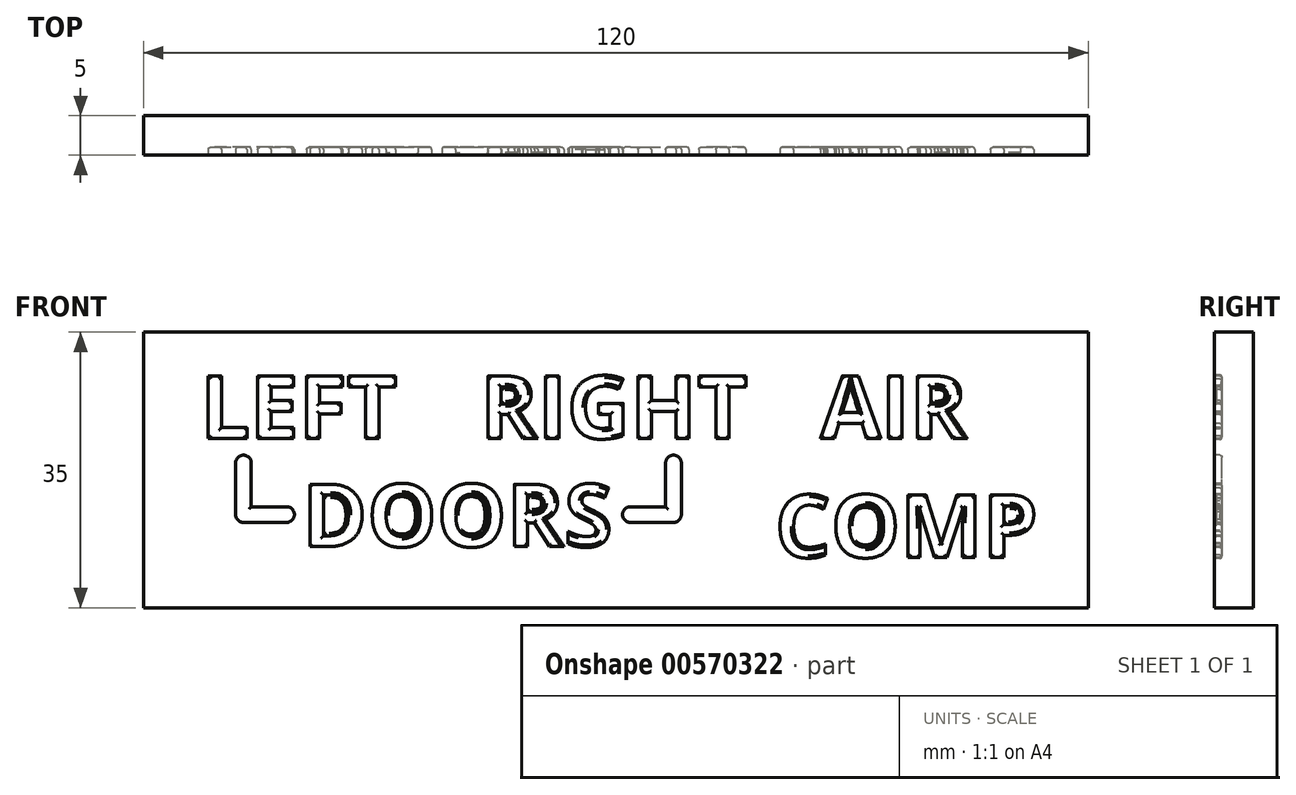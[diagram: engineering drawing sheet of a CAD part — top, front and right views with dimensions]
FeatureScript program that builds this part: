
annotation { "Feature Type Name" : "Feature", "Feature Type Description" : "" }
export const myFeature = defineFeature(function(context is Context, id is Id, definition is map)
    precondition{}
    {
        {
            var Q0;
            Q0=qCreatedBy(makeId("Front.planeOp"),FACE);
            var sketch = newSketch(context, id + "F0", { "sketchPlane" : qUnion([Q0])});
            skLineSegment(sketch, "E0.bottom", {"start": v(60, -17.5) * mm, "end": v(-60, -17.5) * mm});
            skLineSegment(sketch, "E0.top", {"start": v(60, 17.5) * mm, "end": v(-60, 17.5) * mm});
            skLineSegment(sketch, "E0.left", {"start": v(60, -17.5) * mm, "end": v(60, 17.5) * mm});
            skLineSegment(sketch, "E0.right", {"start": v(-60, -17.5) * mm, "end": v(-60, 17.5) * mm});
            skPoint(sketch, "E0.middle", {"position": v(0, 0) * mm});
            skLineSegment(sketch, "E1", {"start": v(-40, 69.11) * mm, "end": v(-40, -88.68) * mm, "construction": true});
            skLineSegment(sketch, "E2", {"start": v(37, 69.11) * mm, "end": v(37, -90.14) * mm, "construction": true});
            skLineSegment(sketch, "E3", {"start": v(0, 69.11) * mm, "end": v(0, -90.14) * mm, "construction": true});
            skSolve(sketch);
        }
        {
            var Q0;
            Q0=makeQuery(id+"F0.imprint","IMPRINT",FACE,{"disambiguationData":[TD([[makeQuery(id+"F0.imprint","IMPRINT",EDGE,{"derivedFrom":sQuery(id+"F0.wireOp",EDGE,"E0.bottom")}),-1.0]])]});
            extrude(context, id + "F1", {"entities" : qUnion([Q0]), "depth" : 5 * mm, "offsetDistance" : 25 * mm});
        }
        {
            var Q0;
            Q0=makeQuery(id+"F1.opExtrude","CAP_FACE",FACE,{"disambiguationData":[OSD([sQuery(id+"F0.wireOp",EDGE,"E0.bottom"),sQuery(id+"F0.wireOp",EDGE,"E0.top"),sQuery(id+"F0.wireOp",EDGE,"E0.left"),sQuery(id+"F0.wireOp",EDGE,"E0.right")])],"isStart":false});
            var sketch = newSketch(context, id + "F2", { "sketchPlane" : qUnion([Q0])});
            skText(sketch, "E4", { "text": "LEFT", "fontName": "OpenSans-Bold.ttf"});
            skText(sketch, "E5", { "text": "DOORS", "fontName": "OpenSans-Bold.ttf"});
            skLineSegment(sketch, "E6", {"start": v(-40, -17.5) * mm, "end": v(0, -17.5) * mm, "construction": true});
            skPoint(sketch, "E7", {"position": v(-20, -17.5) * mm});
            skText(sketch, "E8", { "text": "RIGHT", "fontName": "OpenSans-Bold.ttf"});
            skText(sketch, "E9", { "text": "  AIR\nCOMP", "fontName": "OpenSans-Bold.ttf"});
            skLineSegment(sketch, "E10", {"start": v(-20, -43.15) * mm, "end": v(-20, 45.34) * mm, "construction": true});
            skLineSegment(sketch, "E11", {"start": v(-41.84, -5.67) * mm, "end": v(-47.32, -5.67) * mm});
            skLineSegment(sketch, "E12", {"start": v(-47.32, -5.67) * mm, "end": v(-47.32, 0.89) * mm});
            skLineSegment(sketch, "E13.MirrorCS", {"start": v(7.32, -5.67) * mm, "end": v(7.32, 0.89) * mm});
            skLineSegment(sketch, "E14.MirrorCS", {"start": v(1.84, -5.67) * mm, "end": v(7.32, -5.67) * mm});
            skArc(sketch, "E15.0.startCap", {"start": v(-41.84, -4.67) * mm, "mid": v(-40.84, -5.67) * mm, "end": v(-41.84, -6.67) * mm});
            skArc(sketch, "E15.0.endCap", {"start": v(-47.32, -6.67) * mm, "mid": v(-48.32, -5.67) * mm, "end": v(-47.32, -4.67) * mm});
            skLineSegment(sketch, "E15.0.left", {"start": v(-41.84, -6.67) * mm, "end": v(-47.32, -6.67) * mm});
            skLineSegment(sketch, "E15.0.right", {"start": v(-41.84, -4.67) * mm, "end": v(-47.32, -4.67) * mm});
            skArc(sketch, "E15.1.startCap", {"start": v(-46.32, -5.67) * mm, "mid": v(-47.32, -6.67) * mm, "end": v(-48.32, -5.67) * mm});
            skArc(sketch, "E15.1.endCap", {"start": v(-48.32, 0.89) * mm, "mid": v(-47.32, 1.89) * mm, "end": v(-46.32, 0.89) * mm});
            skLineSegment(sketch, "E15.1.left", {"start": v(-48.32, -5.67) * mm, "end": v(-48.32, 0.89) * mm});
            skLineSegment(sketch, "E15.1.right", {"start": v(-46.32, -5.67) * mm, "end": v(-46.32, 0.89) * mm});
            skArc(sketch, "E15.2.startCap", {"start": v(1.84, -6.67) * mm, "mid": v(0.84, -5.67) * mm, "end": v(1.84, -4.67) * mm});
            skArc(sketch, "E15.2.endCap", {"start": v(7.32, -4.67) * mm, "mid": v(8.32, -5.67) * mm, "end": v(7.32, -6.67) * mm});
            skLineSegment(sketch, "E15.2.left", {"start": v(1.84, -4.67) * mm, "end": v(7.32, -4.67) * mm});
            skLineSegment(sketch, "E15.2.right", {"start": v(1.84, -6.67) * mm, "end": v(7.32, -6.67) * mm});
            skArc(sketch, "E15.3.startCap", {"start": v(8.32, -5.67) * mm, "mid": v(7.32, -6.67) * mm, "end": v(6.32, -5.67) * mm});
            skArc(sketch, "E15.3.endCap", {"start": v(6.32, 0.89) * mm, "mid": v(7.32, 1.89) * mm, "end": v(8.32, 0.89) * mm});
            skLineSegment(sketch, "E15.3.left", {"start": v(6.32, -5.67) * mm, "end": v(6.32, 0.89) * mm});
            skLineSegment(sketch, "E15.3.right", {"start": v(8.32, -5.67) * mm, "end": v(8.32, 0.89) * mm});
            const initialGuessF2  = {"E4": [-0.05277, 0.004, 1, 0, 0.008], "E5": [-0.03982, -0.00974, 1, 0, 0.008], "E8": [-0.01725, 0.004, 1, 0, 0.008], "E9": [0.0202, 0.004, 1, 0, 0.008]};
            skSetInitialGuess(sketch, initialGuessF2);
            skSolve(sketch);
        }
        {
            var Q0;
            Q0 = qSketchRegion(id + "F2", true);
            extrude(context, id + "F3", {"entities" : qUnion([Q0]), "operationType" : NewBodyOperationType.REMOVE, "oppositeDirection" : true, "depth" : 1 * mm, "offsetDistance" : 25 * mm});
        }
        {
            var Q0;
            Q0=makeQuery(id+"F3.boolean.opBoolean","COPY",FACE,{"derivedFrom":makeQuery(id+"F3.opExtrude","CAP_FACE",FACE,{"disambiguationData":[OSD([sQuery(id+"F2.wireOp",EDGE,"E4.sketch_text.stroke-0"),sQuery(id+"F2.wireOp",EDGE,"E4.sketch_text.stroke-1"),sQuery(id+"F2.wireOp",EDGE,"E4.sketch_text.stroke-2"),sQuery(id+"F2.wireOp",EDGE,"E4.sketch_text.stroke-3"),sQuery(id+"F2.wireOp",EDGE,"E4.sketch_text.stroke-4"),sQuery(id+"F2.wireOp",EDGE,"E4.sketch_text.stroke-5")])],"isStart":false})});
            var Q1;
            Q1=makeQuery(id+"F3.boolean.opBoolean","COPY",FACE,{"derivedFrom":makeQuery(id+"F3.opExtrude","CAP_FACE",FACE,{"disambiguationData":[OSD([sQuery(id+"F2.wireOp",EDGE,"E4.sketch_text.stroke-6"),sQuery(id+"F2.wireOp",EDGE,"E4.sketch_text.stroke-7"),sQuery(id+"F2.wireOp",EDGE,"E4.sketch_text.stroke-8"),sQuery(id+"F2.wireOp",EDGE,"E4.sketch_text.stroke-9"),sQuery(id+"F2.wireOp",EDGE,"E4.sketch_text.stroke-10"),sQuery(id+"F2.wireOp",EDGE,"E4.sketch_text.stroke-11"),sQuery(id+"F2.wireOp",EDGE,"E4.sketch_text.stroke-12"),sQuery(id+"F2.wireOp",EDGE,"E4.sketch_text.stroke-13"),sQuery(id+"F2.wireOp",EDGE,"E4.sketch_text.stroke-14"),sQuery(id+"F2.wireOp",EDGE,"E4.sketch_text.stroke-15"),sQuery(id+"F2.wireOp",EDGE,"E4.sketch_text.stroke-16"),sQuery(id+"F2.wireOp",EDGE,"E4.sketch_text.stroke-17")])],"isStart":false})});
            var Q2;
            Q2=makeQuery(id+"F3.boolean.opBoolean","COPY",FACE,{"derivedFrom":makeQuery(id+"F3.opExtrude","CAP_FACE",FACE,{"disambiguationData":[OSD([sQuery(id+"F2.wireOp",EDGE,"E4.sketch_text.stroke-18"),sQuery(id+"F2.wireOp",EDGE,"E4.sketch_text.stroke-19"),sQuery(id+"F2.wireOp",EDGE,"E4.sketch_text.stroke-20"),sQuery(id+"F2.wireOp",EDGE,"E4.sketch_text.stroke-21"),sQuery(id+"F2.wireOp",EDGE,"E4.sketch_text.stroke-22"),sQuery(id+"F2.wireOp",EDGE,"E4.sketch_text.stroke-23"),sQuery(id+"F2.wireOp",EDGE,"E4.sketch_text.stroke-24"),sQuery(id+"F2.wireOp",EDGE,"E4.sketch_text.stroke-25"),sQuery(id+"F2.wireOp",EDGE,"E4.sketch_text.stroke-26"),sQuery(id+"F2.wireOp",EDGE,"E4.sketch_text.stroke-27")])],"isStart":false})});
            var Q3;
            Q3=makeQuery(id+"F3.boolean.opBoolean","COPY",FACE,{"derivedFrom":makeQuery(id+"F3.opExtrude","CAP_FACE",FACE,{"disambiguationData":[OSD([sQuery(id+"F2.wireOp",EDGE,"E4.sketch_text.stroke-28"),sQuery(id+"F2.wireOp",EDGE,"E4.sketch_text.stroke-29"),sQuery(id+"F2.wireOp",EDGE,"E4.sketch_text.stroke-30"),sQuery(id+"F2.wireOp",EDGE,"E4.sketch_text.stroke-31"),sQuery(id+"F2.wireOp",EDGE,"E4.sketch_text.stroke-32"),sQuery(id+"F2.wireOp",EDGE,"E4.sketch_text.stroke-33"),sQuery(id+"F2.wireOp",EDGE,"E4.sketch_text.stroke-34"),sQuery(id+"F2.wireOp",EDGE,"E4.sketch_text.stroke-35")])],"isStart":false})});
            var Q4;
            Q4=makeQuery(id+"F3.boolean.opBoolean","COPY",FACE,{"derivedFrom":makeQuery(id+"F3.opExtrude","CAP_FACE",FACE,{"disambiguationData":[OSD([sQuery(id+"F2.wireOp",EDGE,"E15.0.startCap"),sQuery(id+"F2.wireOp",EDGE,"E15.0.left"),sQuery(id+"F2.wireOp",EDGE,"E15.0.right"),sQuery(id+"F2.wireOp",EDGE,"E15.1.startCap"),sQuery(id+"F2.wireOp",EDGE,"E15.1.endCap"),sQuery(id+"F2.wireOp",EDGE,"E15.1.left"),sQuery(id+"F2.wireOp",EDGE,"E15.1.right")])],"isStart":false})});
            var Q5;
            Q5=makeQuery(id+"F3.boolean.opBoolean","COPY",FACE,{"derivedFrom":makeQuery(id+"F3.opExtrude","CAP_FACE",FACE,{"disambiguationData":[OSD([sQuery(id+"F2.wireOp",EDGE,"E5.sketch_text.stroke-0"),sQuery(id+"F2.wireOp",EDGE,"E5.sketch_text.stroke-1"),sQuery(id+"F2.wireOp",EDGE,"E5.sketch_text.stroke-2"),sQuery(id+"F2.wireOp",EDGE,"E5.sketch_text.stroke-3"),sQuery(id+"F2.wireOp",EDGE,"E5.sketch_text.stroke-4"),sQuery(id+"F2.wireOp",EDGE,"E5.sketch_text.stroke-5"),sQuery(id+"F2.wireOp",EDGE,"E5.sketch_text.stroke-6"),sQuery(id+"F2.wireOp",EDGE,"E5.sketch_text.stroke-7"),sQuery(id+"F2.wireOp",EDGE,"E5.sketch_text.stroke-8"),sQuery(id+"F2.wireOp",EDGE,"E5.sketch_text.stroke-9"),sQuery(id+"F2.wireOp",EDGE,"E5.sketch_text.stroke-10"),sQuery(id+"F2.wireOp",EDGE,"E5.sketch_text.stroke-11")])],"isStart":false})});
            var Q6;
            Q6=makeQuery(id+"F3.boolean.opBoolean","COPY",FACE,{"derivedFrom":makeQuery(id+"F3.opExtrude","CAP_FACE",FACE,{"disambiguationData":[OSD([sQuery(id+"F2.wireOp",EDGE,"E5.sketch_text.stroke-12"),sQuery(id+"F2.wireOp",EDGE,"E5.sketch_text.stroke-13"),sQuery(id+"F2.wireOp",EDGE,"E5.sketch_text.stroke-14"),sQuery(id+"F2.wireOp",EDGE,"E5.sketch_text.stroke-15"),sQuery(id+"F2.wireOp",EDGE,"E5.sketch_text.stroke-16"),sQuery(id+"F2.wireOp",EDGE,"E5.sketch_text.stroke-17"),sQuery(id+"F2.wireOp",EDGE,"E5.sketch_text.stroke-18"),sQuery(id+"F2.wireOp",EDGE,"E5.sketch_text.stroke-19"),sQuery(id+"F2.wireOp",EDGE,"E5.sketch_text.stroke-20"),sQuery(id+"F2.wireOp",EDGE,"E5.sketch_text.stroke-21"),sQuery(id+"F2.wireOp",EDGE,"E5.sketch_text.stroke-22"),sQuery(id+"F2.wireOp",EDGE,"E5.sketch_text.stroke-23"),sQuery(id+"F2.wireOp",EDGE,"E5.sketch_text.stroke-24"),sQuery(id+"F2.wireOp",EDGE,"E5.sketch_text.stroke-25")])],"isStart":false})});
            var Q7;
            Q7=makeQuery(id+"F3.boolean.opBoolean","COPY",FACE,{"derivedFrom":makeQuery(id+"F3.opExtrude","CAP_FACE",FACE,{"disambiguationData":[OSD([sQuery(id+"F2.wireOp",EDGE,"E5.sketch_text.stroke-26"),sQuery(id+"F2.wireOp",EDGE,"E5.sketch_text.stroke-27"),sQuery(id+"F2.wireOp",EDGE,"E5.sketch_text.stroke-28"),sQuery(id+"F2.wireOp",EDGE,"E5.sketch_text.stroke-29"),sQuery(id+"F2.wireOp",EDGE,"E5.sketch_text.stroke-30"),sQuery(id+"F2.wireOp",EDGE,"E5.sketch_text.stroke-31"),sQuery(id+"F2.wireOp",EDGE,"E5.sketch_text.stroke-32"),sQuery(id+"F2.wireOp",EDGE,"E5.sketch_text.stroke-33"),sQuery(id+"F2.wireOp",EDGE,"E5.sketch_text.stroke-34"),sQuery(id+"F2.wireOp",EDGE,"E5.sketch_text.stroke-35"),sQuery(id+"F2.wireOp",EDGE,"E5.sketch_text.stroke-36"),sQuery(id+"F2.wireOp",EDGE,"E5.sketch_text.stroke-37"),sQuery(id+"F2.wireOp",EDGE,"E5.sketch_text.stroke-38"),sQuery(id+"F2.wireOp",EDGE,"E5.sketch_text.stroke-39")])],"isStart":false})});
            var Q8;
            Q8=makeQuery(id+"F3.boolean.opBoolean","COPY",FACE,{"derivedFrom":makeQuery(id+"F3.opExtrude","CAP_FACE",FACE,{"disambiguationData":[OSD([sQuery(id+"F2.wireOp",EDGE,"E8.sketch_text.stroke-0"),sQuery(id+"F2.wireOp",EDGE,"E8.sketch_text.stroke-1"),sQuery(id+"F2.wireOp",EDGE,"E8.sketch_text.stroke-2"),sQuery(id+"F2.wireOp",EDGE,"E8.sketch_text.stroke-3"),sQuery(id+"F2.wireOp",EDGE,"E8.sketch_text.stroke-4"),sQuery(id+"F2.wireOp",EDGE,"E8.sketch_text.stroke-5"),sQuery(id+"F2.wireOp",EDGE,"E8.sketch_text.stroke-6"),sQuery(id+"F2.wireOp",EDGE,"E8.sketch_text.stroke-7"),sQuery(id+"F2.wireOp",EDGE,"E8.sketch_text.stroke-8"),sQuery(id+"F2.wireOp",EDGE,"E8.sketch_text.stroke-9"),sQuery(id+"F2.wireOp",EDGE,"E8.sketch_text.stroke-10"),sQuery(id+"F2.wireOp",EDGE,"E8.sketch_text.stroke-11"),sQuery(id+"F2.wireOp",EDGE,"E8.sketch_text.stroke-12"),sQuery(id+"F2.wireOp",EDGE,"E8.sketch_text.stroke-13"),sQuery(id+"F2.wireOp",EDGE,"E8.sketch_text.stroke-14"),sQuery(id+"F2.wireOp",EDGE,"E8.sketch_text.stroke-15"),sQuery(id+"F2.wireOp",EDGE,"E8.sketch_text.stroke-16"),sQuery(id+"F2.wireOp",EDGE,"E8.sketch_text.stroke-17"),sQuery(id+"F2.wireOp",EDGE,"E8.sketch_text.stroke-18")])],"isStart":false})});
            var Q9;
            Q9=makeQuery(id+"F3.boolean.opBoolean","COPY",FACE,{"derivedFrom":makeQuery(id+"F3.opExtrude","CAP_FACE",FACE,{"disambiguationData":[OSD([sQuery(id+"F2.wireOp",EDGE,"E8.sketch_text.stroke-19"),sQuery(id+"F2.wireOp",EDGE,"E8.sketch_text.stroke-20"),sQuery(id+"F2.wireOp",EDGE,"E8.sketch_text.stroke-21"),sQuery(id+"F2.wireOp",EDGE,"E8.sketch_text.stroke-22")])],"isStart":false})});
            var Q10;
            Q10=makeQuery(id+"F3.boolean.opBoolean","COPY",FACE,{"derivedFrom":makeQuery(id+"F3.opExtrude","CAP_FACE",FACE,{"disambiguationData":[OSD([sQuery(id+"F2.wireOp",EDGE,"E8.sketch_text.stroke-23"),sQuery(id+"F2.wireOp",EDGE,"E8.sketch_text.stroke-24"),sQuery(id+"F2.wireOp",EDGE,"E8.sketch_text.stroke-25"),sQuery(id+"F2.wireOp",EDGE,"E8.sketch_text.stroke-26"),sQuery(id+"F2.wireOp",EDGE,"E8.sketch_text.stroke-27"),sQuery(id+"F2.wireOp",EDGE,"E8.sketch_text.stroke-28"),sQuery(id+"F2.wireOp",EDGE,"E8.sketch_text.stroke-29"),sQuery(id+"F2.wireOp",EDGE,"E8.sketch_text.stroke-30"),sQuery(id+"F2.wireOp",EDGE,"E8.sketch_text.stroke-31"),sQuery(id+"F2.wireOp",EDGE,"E8.sketch_text.stroke-32"),sQuery(id+"F2.wireOp",EDGE,"E8.sketch_text.stroke-33"),sQuery(id+"F2.wireOp",EDGE,"E8.sketch_text.stroke-34"),sQuery(id+"F2.wireOp",EDGE,"E8.sketch_text.stroke-35"),sQuery(id+"F2.wireOp",EDGE,"E8.sketch_text.stroke-36"),sQuery(id+"F2.wireOp",EDGE,"E8.sketch_text.stroke-37"),sQuery(id+"F2.wireOp",EDGE,"E8.sketch_text.stroke-38"),sQuery(id+"F2.wireOp",EDGE,"E8.sketch_text.stroke-39"),sQuery(id+"F2.wireOp",EDGE,"E8.sketch_text.stroke-40"),sQuery(id+"F2.wireOp",EDGE,"E8.sketch_text.stroke-41")])],"isStart":false})});
            var Q11;
            Q11=makeQuery(id+"F3.boolean.opBoolean","COPY",FACE,{"derivedFrom":makeQuery(id+"F3.opExtrude","CAP_FACE",FACE,{"disambiguationData":[OSD([sQuery(id+"F2.wireOp",EDGE,"E5.sketch_text.stroke-40"),sQuery(id+"F2.wireOp",EDGE,"E5.sketch_text.stroke-41"),sQuery(id+"F2.wireOp",EDGE,"E5.sketch_text.stroke-42"),sQuery(id+"F2.wireOp",EDGE,"E5.sketch_text.stroke-43"),sQuery(id+"F2.wireOp",EDGE,"E5.sketch_text.stroke-44"),sQuery(id+"F2.wireOp",EDGE,"E5.sketch_text.stroke-45"),sQuery(id+"F2.wireOp",EDGE,"E5.sketch_text.stroke-46"),sQuery(id+"F2.wireOp",EDGE,"E5.sketch_text.stroke-47"),sQuery(id+"F2.wireOp",EDGE,"E5.sketch_text.stroke-48"),sQuery(id+"F2.wireOp",EDGE,"E5.sketch_text.stroke-49"),sQuery(id+"F2.wireOp",EDGE,"E5.sketch_text.stroke-50"),sQuery(id+"F2.wireOp",EDGE,"E5.sketch_text.stroke-51"),sQuery(id+"F2.wireOp",EDGE,"E5.sketch_text.stroke-52"),sQuery(id+"F2.wireOp",EDGE,"E5.sketch_text.stroke-53"),sQuery(id+"F2.wireOp",EDGE,"E5.sketch_text.stroke-54"),sQuery(id+"F2.wireOp",EDGE,"E5.sketch_text.stroke-55"),sQuery(id+"F2.wireOp",EDGE,"E5.sketch_text.stroke-56"),sQuery(id+"F2.wireOp",EDGE,"E5.sketch_text.stroke-57"),sQuery(id+"F2.wireOp",EDGE,"E5.sketch_text.stroke-58")])],"isStart":false})});
            var Q12;
            Q12=makeQuery(id+"F3.boolean.opBoolean","COPY",FACE,{"derivedFrom":makeQuery(id+"F3.opExtrude","CAP_FACE",FACE,{"disambiguationData":[OSD([sQuery(id+"F2.wireOp",EDGE,"E5.sketch_text.stroke-59"),sQuery(id+"F2.wireOp",EDGE,"E5.sketch_text.stroke-60"),sQuery(id+"F2.wireOp",EDGE,"E5.sketch_text.stroke-61"),sQuery(id+"F2.wireOp",EDGE,"E5.sketch_text.stroke-62"),sQuery(id+"F2.wireOp",EDGE,"E5.sketch_text.stroke-63"),sQuery(id+"F2.wireOp",EDGE,"E5.sketch_text.stroke-64"),sQuery(id+"F2.wireOp",EDGE,"E5.sketch_text.stroke-65"),sQuery(id+"F2.wireOp",EDGE,"E5.sketch_text.stroke-66"),sQuery(id+"F2.wireOp",EDGE,"E5.sketch_text.stroke-67"),sQuery(id+"F2.wireOp",EDGE,"E5.sketch_text.stroke-68"),sQuery(id+"F2.wireOp",EDGE,"E5.sketch_text.stroke-69"),sQuery(id+"F2.wireOp",EDGE,"E5.sketch_text.stroke-70"),sQuery(id+"F2.wireOp",EDGE,"E5.sketch_text.stroke-71"),sQuery(id+"F2.wireOp",EDGE,"E5.sketch_text.stroke-72"),sQuery(id+"F2.wireOp",EDGE,"E5.sketch_text.stroke-73"),sQuery(id+"F2.wireOp",EDGE,"E5.sketch_text.stroke-74"),sQuery(id+"F2.wireOp",EDGE,"E5.sketch_text.stroke-75"),sQuery(id+"F2.wireOp",EDGE,"E5.sketch_text.stroke-76"),sQuery(id+"F2.wireOp",EDGE,"E5.sketch_text.stroke-77"),sQuery(id+"F2.wireOp",EDGE,"E5.sketch_text.stroke-78"),sQuery(id+"F2.wireOp",EDGE,"E5.sketch_text.stroke-79"),sQuery(id+"F2.wireOp",EDGE,"E5.sketch_text.stroke-80"),sQuery(id+"F2.wireOp",EDGE,"E5.sketch_text.stroke-81"),sQuery(id+"F2.wireOp",EDGE,"E5.sketch_text.stroke-82"),sQuery(id+"F2.wireOp",EDGE,"E5.sketch_text.stroke-83"),sQuery(id+"F2.wireOp",EDGE,"E5.sketch_text.stroke-84"),sQuery(id+"F2.wireOp",EDGE,"E5.sketch_text.stroke-85"),sQuery(id+"F2.wireOp",EDGE,"E5.sketch_text.stroke-86")])],"isStart":false})});
            var Q13;
            Q13=makeQuery(id+"F3.boolean.opBoolean","COPY",FACE,{"derivedFrom":makeQuery(id+"F3.opExtrude","CAP_FACE",FACE,{"disambiguationData":[OSD([sQuery(id+"F2.wireOp",EDGE,"E15.2.startCap"),sQuery(id+"F2.wireOp",EDGE,"E15.2.left"),sQuery(id+"F2.wireOp",EDGE,"E15.2.right"),sQuery(id+"F2.wireOp",EDGE,"E15.3.startCap"),sQuery(id+"F2.wireOp",EDGE,"E15.3.endCap"),sQuery(id+"F2.wireOp",EDGE,"E15.3.left"),sQuery(id+"F2.wireOp",EDGE,"E15.3.right")])],"isStart":false})});
            var Q14;
            Q14=makeQuery(id+"F3.boolean.opBoolean","COPY",FACE,{"derivedFrom":makeQuery(id+"F3.opExtrude","CAP_FACE",FACE,{"disambiguationData":[OSD([sQuery(id+"F2.wireOp",EDGE,"E8.sketch_text.stroke-42"),sQuery(id+"F2.wireOp",EDGE,"E8.sketch_text.stroke-43"),sQuery(id+"F2.wireOp",EDGE,"E8.sketch_text.stroke-44"),sQuery(id+"F2.wireOp",EDGE,"E8.sketch_text.stroke-45"),sQuery(id+"F2.wireOp",EDGE,"E8.sketch_text.stroke-46"),sQuery(id+"F2.wireOp",EDGE,"E8.sketch_text.stroke-47"),sQuery(id+"F2.wireOp",EDGE,"E8.sketch_text.stroke-48"),sQuery(id+"F2.wireOp",EDGE,"E8.sketch_text.stroke-49"),sQuery(id+"F2.wireOp",EDGE,"E8.sketch_text.stroke-50"),sQuery(id+"F2.wireOp",EDGE,"E8.sketch_text.stroke-51"),sQuery(id+"F2.wireOp",EDGE,"E8.sketch_text.stroke-52"),sQuery(id+"F2.wireOp",EDGE,"E8.sketch_text.stroke-53")])],"isStart":false})});
            var Q15;
            Q15=makeQuery(id+"F3.boolean.opBoolean","COPY",FACE,{"derivedFrom":makeQuery(id+"F3.opExtrude","CAP_FACE",FACE,{"disambiguationData":[OSD([sQuery(id+"F2.wireOp",EDGE,"E8.sketch_text.stroke-54"),sQuery(id+"F2.wireOp",EDGE,"E8.sketch_text.stroke-55"),sQuery(id+"F2.wireOp",EDGE,"E8.sketch_text.stroke-56"),sQuery(id+"F2.wireOp",EDGE,"E8.sketch_text.stroke-57"),sQuery(id+"F2.wireOp",EDGE,"E8.sketch_text.stroke-58"),sQuery(id+"F2.wireOp",EDGE,"E8.sketch_text.stroke-59"),sQuery(id+"F2.wireOp",EDGE,"E8.sketch_text.stroke-60"),sQuery(id+"F2.wireOp",EDGE,"E8.sketch_text.stroke-61")])],"isStart":false})});
            var Q16;
            Q16=makeQuery(id+"F3.boolean.opBoolean","COPY",FACE,{"derivedFrom":makeQuery(id+"F3.opExtrude","CAP_FACE",FACE,{"disambiguationData":[OSD([sQuery(id+"F2.wireOp",EDGE,"E9.sketch_text.stroke-0"),sQuery(id+"F2.wireOp",EDGE,"E9.sketch_text.stroke-1"),sQuery(id+"F2.wireOp",EDGE,"E9.sketch_text.stroke-2"),sQuery(id+"F2.wireOp",EDGE,"E9.sketch_text.stroke-3"),sQuery(id+"F2.wireOp",EDGE,"E9.sketch_text.stroke-4"),sQuery(id+"F2.wireOp",EDGE,"E9.sketch_text.stroke-5"),sQuery(id+"F2.wireOp",EDGE,"E9.sketch_text.stroke-6"),sQuery(id+"F2.wireOp",EDGE,"E9.sketch_text.stroke-7"),sQuery(id+"F2.wireOp",EDGE,"E9.sketch_text.stroke-8"),sQuery(id+"F2.wireOp",EDGE,"E9.sketch_text.stroke-9"),sQuery(id+"F2.wireOp",EDGE,"E9.sketch_text.stroke-10"),sQuery(id+"F2.wireOp",EDGE,"E9.sketch_text.stroke-11")])],"isStart":false})});
            var Q17;
            Q17=makeQuery(id+"F3.boolean.opBoolean","COPY",FACE,{"derivedFrom":makeQuery(id+"F3.opExtrude","CAP_FACE",FACE,{"disambiguationData":[OSD([sQuery(id+"F2.wireOp",EDGE,"E9.sketch_text.stroke-12"),sQuery(id+"F2.wireOp",EDGE,"E9.sketch_text.stroke-13"),sQuery(id+"F2.wireOp",EDGE,"E9.sketch_text.stroke-14"),sQuery(id+"F2.wireOp",EDGE,"E9.sketch_text.stroke-15")])],"isStart":false})});
            var Q18;
            Q18=makeQuery(id+"F3.boolean.opBoolean","COPY",FACE,{"derivedFrom":makeQuery(id+"F3.opExtrude","CAP_FACE",FACE,{"disambiguationData":[OSD([sQuery(id+"F2.wireOp",EDGE,"E9.sketch_text.stroke-16"),sQuery(id+"F2.wireOp",EDGE,"E9.sketch_text.stroke-17"),sQuery(id+"F2.wireOp",EDGE,"E9.sketch_text.stroke-18"),sQuery(id+"F2.wireOp",EDGE,"E9.sketch_text.stroke-19"),sQuery(id+"F2.wireOp",EDGE,"E9.sketch_text.stroke-20"),sQuery(id+"F2.wireOp",EDGE,"E9.sketch_text.stroke-21"),sQuery(id+"F2.wireOp",EDGE,"E9.sketch_text.stroke-22"),sQuery(id+"F2.wireOp",EDGE,"E9.sketch_text.stroke-23"),sQuery(id+"F2.wireOp",EDGE,"E9.sketch_text.stroke-24"),sQuery(id+"F2.wireOp",EDGE,"E9.sketch_text.stroke-25"),sQuery(id+"F2.wireOp",EDGE,"E9.sketch_text.stroke-26"),sQuery(id+"F2.wireOp",EDGE,"E9.sketch_text.stroke-27"),sQuery(id+"F2.wireOp",EDGE,"E9.sketch_text.stroke-28"),sQuery(id+"F2.wireOp",EDGE,"E9.sketch_text.stroke-29"),sQuery(id+"F2.wireOp",EDGE,"E9.sketch_text.stroke-30"),sQuery(id+"F2.wireOp",EDGE,"E9.sketch_text.stroke-31"),sQuery(id+"F2.wireOp",EDGE,"E9.sketch_text.stroke-32"),sQuery(id+"F2.wireOp",EDGE,"E9.sketch_text.stroke-33"),sQuery(id+"F2.wireOp",EDGE,"E9.sketch_text.stroke-34")])],"isStart":false})});
            var Q19;
            Q19=makeQuery(id+"F3.boolean.opBoolean","COPY",FACE,{"derivedFrom":makeQuery(id+"F3.opExtrude","CAP_FACE",FACE,{"disambiguationData":[OSD([sQuery(id+"F2.wireOp",EDGE,"E9.sketch_text.stroke-64"),sQuery(id+"F2.wireOp",EDGE,"E9.sketch_text.stroke-65"),sQuery(id+"F2.wireOp",EDGE,"E9.sketch_text.stroke-66"),sQuery(id+"F2.wireOp",EDGE,"E9.sketch_text.stroke-67"),sQuery(id+"F2.wireOp",EDGE,"E9.sketch_text.stroke-68"),sQuery(id+"F2.wireOp",EDGE,"E9.sketch_text.stroke-69"),sQuery(id+"F2.wireOp",EDGE,"E9.sketch_text.stroke-70"),sQuery(id+"F2.wireOp",EDGE,"E9.sketch_text.stroke-71"),sQuery(id+"F2.wireOp",EDGE,"E9.sketch_text.stroke-72"),sQuery(id+"F2.wireOp",EDGE,"E9.sketch_text.stroke-73"),sQuery(id+"F2.wireOp",EDGE,"E9.sketch_text.stroke-74"),sQuery(id+"F2.wireOp",EDGE,"E9.sketch_text.stroke-75"),sQuery(id+"F2.wireOp",EDGE,"E9.sketch_text.stroke-76"),sQuery(id+"F2.wireOp",EDGE,"E9.sketch_text.stroke-77"),sQuery(id+"F2.wireOp",EDGE,"E9.sketch_text.stroke-78"),sQuery(id+"F2.wireOp",EDGE,"E9.sketch_text.stroke-79"),sQuery(id+"F2.wireOp",EDGE,"E9.sketch_text.stroke-80"),sQuery(id+"F2.wireOp",EDGE,"E9.sketch_text.stroke-81"),sQuery(id+"F2.wireOp",EDGE,"E9.sketch_text.stroke-82")])],"isStart":false})});
            var Q20;
            Q20=makeQuery(id+"F3.boolean.opBoolean","COPY",FACE,{"derivedFrom":makeQuery(id+"F3.opExtrude","CAP_FACE",FACE,{"disambiguationData":[OSD([sQuery(id+"F2.wireOp",EDGE,"E9.sketch_text.stroke-50"),sQuery(id+"F2.wireOp",EDGE,"E9.sketch_text.stroke-51"),sQuery(id+"F2.wireOp",EDGE,"E9.sketch_text.stroke-52"),sQuery(id+"F2.wireOp",EDGE,"E9.sketch_text.stroke-53"),sQuery(id+"F2.wireOp",EDGE,"E9.sketch_text.stroke-54"),sQuery(id+"F2.wireOp",EDGE,"E9.sketch_text.stroke-55"),sQuery(id+"F2.wireOp",EDGE,"E9.sketch_text.stroke-56"),sQuery(id+"F2.wireOp",EDGE,"E9.sketch_text.stroke-57"),sQuery(id+"F2.wireOp",EDGE,"E9.sketch_text.stroke-58"),sQuery(id+"F2.wireOp",EDGE,"E9.sketch_text.stroke-59"),sQuery(id+"F2.wireOp",EDGE,"E9.sketch_text.stroke-60"),sQuery(id+"F2.wireOp",EDGE,"E9.sketch_text.stroke-61"),sQuery(id+"F2.wireOp",EDGE,"E9.sketch_text.stroke-62"),sQuery(id+"F2.wireOp",EDGE,"E9.sketch_text.stroke-63")])],"isStart":false})});
            var Q21;
            Q21=makeQuery(id+"F3.boolean.opBoolean","COPY",FACE,{"derivedFrom":makeQuery(id+"F3.opExtrude","CAP_FACE",FACE,{"disambiguationData":[OSD([sQuery(id+"F2.wireOp",EDGE,"E9.sketch_text.stroke-35"),sQuery(id+"F2.wireOp",EDGE,"E9.sketch_text.stroke-36"),sQuery(id+"F2.wireOp",EDGE,"E9.sketch_text.stroke-37"),sQuery(id+"F2.wireOp",EDGE,"E9.sketch_text.stroke-38"),sQuery(id+"F2.wireOp",EDGE,"E9.sketch_text.stroke-39"),sQuery(id+"F2.wireOp",EDGE,"E9.sketch_text.stroke-40"),sQuery(id+"F2.wireOp",EDGE,"E9.sketch_text.stroke-41"),sQuery(id+"F2.wireOp",EDGE,"E9.sketch_text.stroke-42"),sQuery(id+"F2.wireOp",EDGE,"E9.sketch_text.stroke-43"),sQuery(id+"F2.wireOp",EDGE,"E9.sketch_text.stroke-44"),sQuery(id+"F2.wireOp",EDGE,"E9.sketch_text.stroke-45"),sQuery(id+"F2.wireOp",EDGE,"E9.sketch_text.stroke-46"),sQuery(id+"F2.wireOp",EDGE,"E9.sketch_text.stroke-47"),sQuery(id+"F2.wireOp",EDGE,"E9.sketch_text.stroke-48"),sQuery(id+"F2.wireOp",EDGE,"E9.sketch_text.stroke-49")])],"isStart":false})});
            var Q22;
            Q22=makeQuery(id+"F3.boolean.opBoolean","COPY",FACE,{"derivedFrom":makeQuery(id+"F3.opExtrude","CAP_FACE",FACE,{"disambiguationData":[OSD([sQuery(id+"F2.wireOp",EDGE,"E9.sketch_text.stroke-83"),sQuery(id+"F2.wireOp",EDGE,"E9.sketch_text.stroke-84"),sQuery(id+"F2.wireOp",EDGE,"E9.sketch_text.stroke-85"),sQuery(id+"F2.wireOp",EDGE,"E9.sketch_text.stroke-86"),sQuery(id+"F2.wireOp",EDGE,"E9.sketch_text.stroke-87"),sQuery(id+"F2.wireOp",EDGE,"E9.sketch_text.stroke-88"),sQuery(id+"F2.wireOp",EDGE,"E9.sketch_text.stroke-89"),sQuery(id+"F2.wireOp",EDGE,"E9.sketch_text.stroke-90"),sQuery(id+"F2.wireOp",EDGE,"E9.sketch_text.stroke-91"),sQuery(id+"F2.wireOp",EDGE,"E9.sketch_text.stroke-92"),sQuery(id+"F2.wireOp",EDGE,"E9.sketch_text.stroke-93"),sQuery(id+"F2.wireOp",EDGE,"E9.sketch_text.stroke-94"),sQuery(id+"F2.wireOp",EDGE,"E9.sketch_text.stroke-95"),sQuery(id+"F2.wireOp",EDGE,"E9.sketch_text.stroke-96"),sQuery(id+"F2.wireOp",EDGE,"E9.sketch_text.stroke-97"),sQuery(id+"F2.wireOp",EDGE,"E9.sketch_text.stroke-98")])],"isStart":false})});
            fillet(context, id + "F4", {"entities" : qUnion([Q0, Q1, Q2, Q3, Q4, Q5, Q6, Q7, Q8, Q9, Q10, Q11, Q12, Q13, Q14, Q15, Q16, Q17, Q18, Q19, Q20, Q21, Q22]), "radius" : .3 * mm, "tangentPropagation" : true, "allowEdgeOverflow" : false});
        }
        {
            var Q0;
            Q0=makeQuery(id+"F3.boolean.opBoolean","SPLIT",FACE,{"disambiguationData":[TD([makeQuery(id+"F3.opExtrude","SWEPT_FACE",FACE,{"disambiguationData":[OSD([sQuery(id+"F2.wireOp",EDGE,"E5.sketch_text.stroke-20")])]})])],"derivedFrom":makeQuery(id+"F1.opExtrude","CAP_FACE",FACE,{"disambiguationData":[OSD([sQuery(id+"F0.wireOp",EDGE,"E0.bottom"),sQuery(id+"F0.wireOp",EDGE,"E0.top"),sQuery(id+"F0.wireOp",EDGE,"E0.left"),sQuery(id+"F0.wireOp",EDGE,"E0.right")])],"isStart":false})});
            var Q1;
            Q1=makeQuery(id+"F3.boolean.opBoolean","SPLIT",FACE,{"disambiguationData":[TD([makeQuery(id+"F3.opExtrude","SWEPT_FACE",FACE,{"disambiguationData":[OSD([sQuery(id+"F2.wireOp",EDGE,"E5.sketch_text.stroke-7")])]})])],"derivedFrom":makeQuery(id+"F1.opExtrude","CAP_FACE",FACE,{"disambiguationData":[OSD([sQuery(id+"F0.wireOp",EDGE,"E0.bottom"),sQuery(id+"F0.wireOp",EDGE,"E0.top"),sQuery(id+"F0.wireOp",EDGE,"E0.left"),sQuery(id+"F0.wireOp",EDGE,"E0.right")])],"isStart":false})});
            var Q2;
            Q2=makeQuery(id+"F3.boolean.opBoolean","SPLIT",FACE,{"disambiguationData":[TD([makeQuery(id+"F3.opExtrude","SWEPT_FACE",FACE,{"disambiguationData":[OSD([sQuery(id+"F2.wireOp",EDGE,"E5.sketch_text.stroke-34")])]})])],"derivedFrom":makeQuery(id+"F1.opExtrude","CAP_FACE",FACE,{"disambiguationData":[OSD([sQuery(id+"F0.wireOp",EDGE,"E0.bottom"),sQuery(id+"F0.wireOp",EDGE,"E0.top"),sQuery(id+"F0.wireOp",EDGE,"E0.left"),sQuery(id+"F0.wireOp",EDGE,"E0.right")])],"isStart":false})});
            var Q3;
            Q3=makeQuery(id+"F3.boolean.opBoolean","SPLIT",FACE,{"disambiguationData":[TD([makeQuery(id+"F3.opExtrude","SWEPT_FACE",FACE,{"disambiguationData":[OSD([sQuery(id+"F2.wireOp",EDGE,"E5.sketch_text.stroke-40")])]})])],"derivedFrom":makeQuery(id+"F1.opExtrude","CAP_FACE",FACE,{"disambiguationData":[OSD([sQuery(id+"F0.wireOp",EDGE,"E0.bottom"),sQuery(id+"F0.wireOp",EDGE,"E0.top"),sQuery(id+"F0.wireOp",EDGE,"E0.left"),sQuery(id+"F0.wireOp",EDGE,"E0.right")])],"isStart":false})});
            var Q4;
            Q4=makeQuery(id+"F3.boolean.opBoolean","SPLIT",FACE,{"disambiguationData":[TD([makeQuery(id+"F3.opExtrude","SWEPT_FACE",FACE,{"disambiguationData":[OSD([sQuery(id+"F2.wireOp",EDGE,"E8.sketch_text.stroke-0")])]})])],"derivedFrom":makeQuery(id+"F1.opExtrude","CAP_FACE",FACE,{"disambiguationData":[OSD([sQuery(id+"F0.wireOp",EDGE,"E0.bottom"),sQuery(id+"F0.wireOp",EDGE,"E0.top"),sQuery(id+"F0.wireOp",EDGE,"E0.left"),sQuery(id+"F0.wireOp",EDGE,"E0.right")])],"isStart":false})});
            var Q5;
            Q5=makeQuery(id+"F3.boolean.opBoolean","SPLIT",FACE,{"disambiguationData":[TD([makeQuery(id+"F3.opExtrude","SWEPT_FACE",FACE,{"disambiguationData":[OSD([sQuery(id+"F2.wireOp",EDGE,"E9.sketch_text.stroke-16")])]})])],"derivedFrom":makeQuery(id+"F1.opExtrude","CAP_FACE",FACE,{"disambiguationData":[OSD([sQuery(id+"F0.wireOp",EDGE,"E0.bottom"),sQuery(id+"F0.wireOp",EDGE,"E0.top"),sQuery(id+"F0.wireOp",EDGE,"E0.left"),sQuery(id+"F0.wireOp",EDGE,"E0.right")])],"isStart":false})});
            var Q6;
            Q6=makeQuery(id+"F3.boolean.opBoolean","SPLIT",FACE,{"disambiguationData":[TD([makeQuery(id+"F3.opExtrude","SWEPT_FACE",FACE,{"disambiguationData":[OSD([sQuery(id+"F2.wireOp",EDGE,"E9.sketch_text.stroke-83")])]})])],"derivedFrom":makeQuery(id+"F1.opExtrude","CAP_FACE",FACE,{"disambiguationData":[OSD([sQuery(id+"F0.wireOp",EDGE,"E0.bottom"),sQuery(id+"F0.wireOp",EDGE,"E0.top"),sQuery(id+"F0.wireOp",EDGE,"E0.left"),sQuery(id+"F0.wireOp",EDGE,"E0.right")])],"isStart":false})});
            var Q7;
            Q7=makeQuery(id+"F3.boolean.opBoolean","SPLIT",FACE,{"disambiguationData":[TD([makeQuery(id+"F3.opExtrude","SWEPT_FACE",FACE,{"disambiguationData":[OSD([sQuery(id+"F2.wireOp",EDGE,"E9.sketch_text.stroke-58")])]})])],"derivedFrom":makeQuery(id+"F1.opExtrude","CAP_FACE",FACE,{"disambiguationData":[OSD([sQuery(id+"F0.wireOp",EDGE,"E0.bottom"),sQuery(id+"F0.wireOp",EDGE,"E0.top"),sQuery(id+"F0.wireOp",EDGE,"E0.left"),sQuery(id+"F0.wireOp",EDGE,"E0.right")])],"isStart":false})});
            fillet(context, id + "F5", {"entities" : qUnion([Q0, Q1, Q2, Q3, Q4, Q5, Q6, Q7]), "radius" : .3 * mm, "tangentPropagation" : true, "allowEdgeOverflow" : false});
        }
    });
